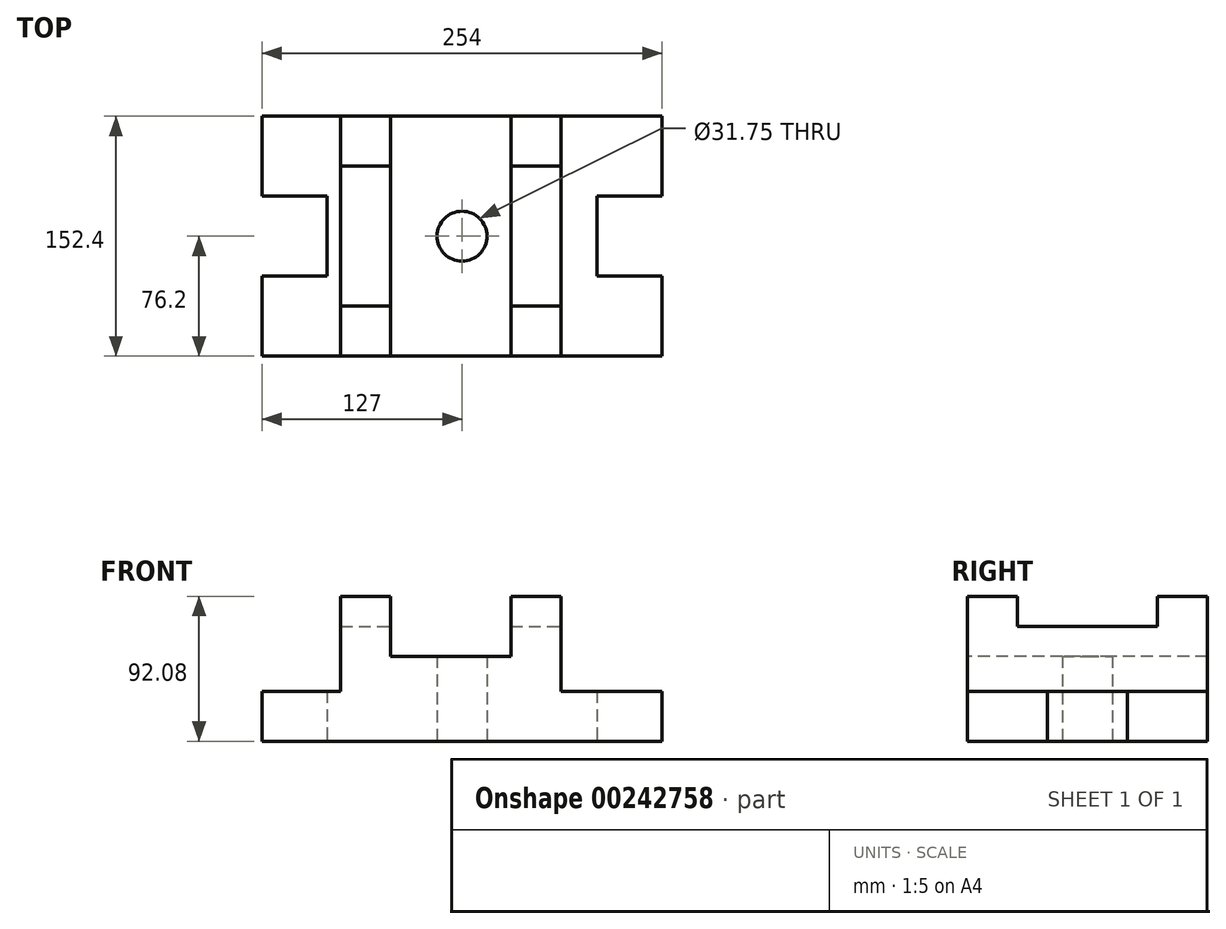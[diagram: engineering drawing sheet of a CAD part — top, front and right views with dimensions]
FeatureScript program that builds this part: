
annotation { "Feature Type Name" : "Feature", "Feature Type Description" : "" }
export const myFeature = defineFeature(function(context is Context, id is Id, definition is map)
    precondition{}
    {
        {
            var Q0;
            Q0=qCreatedBy(makeId("Top.planeOp"),FACE);
            var sketch = newSketch(context, id + "F0", { "sketchPlane" : qUnion([Q0])});
            skLineSegment(sketch, "E0.bottom", {"start": v(127, -76.2) * mm, "end": v(-127, -76.2) * mm});
            skLineSegment(sketch, "E0.top", {"start": v(127, 76.2) * mm, "end": v(-127, 76.2) * mm});
            skLineSegment(sketch, "E0.left", {"start": v(127, -76.2) * mm, "end": v(127, -25.4) * mm});
            skLineSegment(sketch, "E0.right", {"start": v(-127, -76.2) * mm, "end": v(-127, -25.4) * mm});
            skPoint(sketch, "E0.middle", {"position": v(0, 0) * mm});
            skLineSegment(sketch, "E1.bottom", {"start": v(-127, -25.4) * mm, "end": v(-85.72, -25.4) * mm});
            skLineSegment(sketch, "E1.top", {"start": v(-127, 25.4) * mm, "end": v(-85.72, 25.4) * mm});
            skLineSegment(sketch, "E1.right", {"start": v(-85.72, -25.4) * mm, "end": v(-85.72, 25.4) * mm});
            skPoint(sketch, "E1.middle", {"position": v(-106.36, 0) * mm});
            skLineSegment(sketch, "E2.bottom", {"start": v(127, -25.4) * mm, "end": v(85.72, -25.4) * mm});
            skLineSegment(sketch, "E2.top", {"start": v(127, 25.4) * mm, "end": v(85.72, 25.4) * mm});
            skLineSegment(sketch, "E2.right", {"start": v(85.72, -25.4) * mm, "end": v(85.72, 25.4) * mm});
            skPoint(sketch, "E2.middle", {"position": v(106.36, 0) * mm});
            skLineSegment(sketch, "E3.trimOffspring", {"start": v(-127, 25.4) * mm, "end": v(-127, 76.2) * mm});
            skLineSegment(sketch, "E4.trimOffspring", {"start": v(127, 25.4) * mm, "end": v(127, 76.2) * mm});
            skCircle(sketch, "E5", {"center": v(0, 0) * mm, "radius": 15.88 * mm});
            skLineSegment(sketch, "E6", {"start": v(0, 81.37) * mm, "end": v(0, 15.88) * mm, "construction": true});
            skPoint(sketch, "E6.endSnap0", {"position": v(0, -76.2) * mm});
            skLineSegment(sketch, "E7", {"start": v(-183.77, 0) * mm, "end": v(-15.88, 0) * mm, "construction": true});
            skLineSegment(sketch, "E8.trimOffspring", {"start": v(15.88, 0) * mm, "end": v(190.43, 0) * mm, "construction": true});
            skLineSegment(sketch, "E9.trimOffspring", {"start": v(0, 0) * mm, "end": v(0, -121.78) * mm, "construction": true});
            skSolve(sketch);
        }
        {
            var Q0;
            Q0=qCreatedBy(makeId("Front.planeOp"),FACE);
            var sketch = newSketch(context, id + "F1", { "sketchPlane" : qUnion([Q0])});
            skLineSegment(sketch, "E10.top", {"start": v(-77, 92.08) * mm, "end": v(-45.24, 92.08) * mm});
            skLineSegment(sketch, "E10.left", {"start": v(-77, 31.75) * mm, "end": v(-77, 92.08) * mm});
            skLineSegment(sketch, "E11.top", {"start": v(-45.24, 53.98) * mm, "end": v(0, 53.98) * mm});
            skLineSegment(sketch, "E11.left", {"start": v(-45.24, 92.08) * mm, "end": v(-45.24, 53.98) * mm});
            skPoint(sketch, "E12", {"position": v(-45.24, 92.08) * mm});
            skLineSegment(sketch, "E13.MirrorCS", {"start": v(30.96, 92.08) * mm, "end": v(30.96, 53.98) * mm});
            skLineSegment(sketch, "E14.MirrorCS", {"start": v(30.96, 53.98) * mm, "end": v(0, 53.98) * mm});
            skLineSegment(sketch, "E15.MirrorCS", {"start": v(62.7, 31.75) * mm, "end": v(62.7, 92.08) * mm});
            skLineSegment(sketch, "E16.MirrorCS", {"start": v(62.7, 92.08) * mm, "end": v(30.96, 92.08) * mm});
            skPoint(sketch, "E17.MirrorP", {"position": v(30.96, 92.08) * mm});
            skLineSegment(sketch, "E18", {"start": v(-77, 31.75) * mm, "end": v(62.7, 31.75) * mm});
            skSolve(sketch);
        }
        {
            var Q0;
            Q0=makeQuery(id+"F0.imprint","IMPRINT",FACE,{"disambiguationData":[TD([[makeQuery(id+"F0.imprint","IMPRINT",EDGE,{"derivedFrom":sQuery(id+"F0.wireOp",EDGE,"E0.bottom")}),-1.0]])]});
            extrude(context, id + "F2", {"entities" : qUnion([Q0]), "depth" : 31.75 * mm});
        }
        {
            var Q0;
            Q0 = qSketchRegion(id + "F1", true);
            extrude(context, id + "F3", {"entities" : qUnion([Q0]), "operationType" : NewBodyOperationType.ADD, "endBound" : BoundingType.SYMMETRIC, "oppositeDirection" : true, "depth" : 152.4 * mm});
        }
        {
            var Q0;
            Q0=makeQuery(id+"F3.opExtrude","SWEPT_FACE",FACE,{"disambiguationData":[OSD([sQuery(id+"F1.wireOp",EDGE,"E10.top")])]});
            var sketch = newSketch(context, id + "F4", { "sketchPlane" : qUnion([Q0])});
            skLineSegment(sketch, "E19.bottom", {"start": v(-77, 76.2) * mm, "end": v(-45.24, 76.2) * mm});
            skLineSegment(sketch, "E19.top", {"start": v(-77, 44.45) * mm, "end": v(-45.24, 44.45) * mm});
            skLineSegment(sketch, "E19.left", {"start": v(-77, 76.2) * mm, "end": v(-77, 44.45) * mm});
            skLineSegment(sketch, "E19.right", {"start": v(-45.24, 76.2) * mm, "end": v(-45.24, 44.45) * mm});
            skLineSegment(sketch, "E20.bottom", {"start": v(-77, -44.45) * mm, "end": v(-45.24, -44.45) * mm});
            skLineSegment(sketch, "E20.top", {"start": v(-77, -76.2) * mm, "end": v(-45.24, -76.2) * mm});
            skLineSegment(sketch, "E20.left", {"start": v(-77, -44.45) * mm, "end": v(-77, -76.2) * mm});
            skLineSegment(sketch, "E20.right", {"start": v(-45.24, -44.45) * mm, "end": v(-45.24, -76.2) * mm});
            skLineSegment(sketch, "E21.bottom", {"start": v(30.96, 76.2) * mm, "end": v(62.7, 76.2) * mm});
            skLineSegment(sketch, "E21.top", {"start": v(30.96, 44.45) * mm, "end": v(62.7, 44.45) * mm});
            skLineSegment(sketch, "E21.left", {"start": v(30.96, 76.2) * mm, "end": v(30.96, 44.45) * mm});
            skLineSegment(sketch, "E21.right", {"start": v(62.7, 76.2) * mm, "end": v(62.7, 44.45) * mm});
            skLineSegment(sketch, "E22.bottom", {"start": v(30.96, -76.2) * mm, "end": v(62.7, -76.2) * mm});
            skLineSegment(sketch, "E22.top", {"start": v(30.96, -44.45) * mm, "end": v(62.7, -44.45) * mm});
            skLineSegment(sketch, "E22.left", {"start": v(30.96, -76.2) * mm, "end": v(30.96, -44.45) * mm});
            skLineSegment(sketch, "E22.right", {"start": v(62.7, -76.2) * mm, "end": v(62.7, -44.45) * mm});
            skLineSegment(sketch, "E23.left", {"start": v(30.96, 44.45) * mm, "end": v(30.96, -44.45) * mm});
            skLineSegment(sketch, "E23.right", {"start": v(62.7, 44.45) * mm, "end": v(62.7, -44.45) * mm});
            skSolve(sketch);
        }
        {
            var Q0;
            {var subQ0=sQuery(id+"F4.wireOp",EDGE,"E19.top");Q0=makeQuery(id+"F4.imprint","IMPRINT",FACE,{"disambiguationData":[TD([[makeQuery(id+"F4.imprint","IMPRINT",EDGE,{"derivedFrom":subQ0}),-1.0]])]});}
            var Q1;
            Q1=makeQuery(id+"F4.imprint","IMPRINT",FACE,{"disambiguationData":[TD([[makeQuery(id+"F4.imprint","IMPRINT",EDGE,{"derivedFrom":sQuery(id+"F4.wireOp",EDGE,"E21.top")}),-1.0]])]});
            extrude(context, id + "F5", {"entities" : qUnion([Q0, Q1]), "operationType" : NewBodyOperationType.REMOVE, "oppositeDirection" : true, "depth" : 19.05 * mm});
        }
        {
            var Q0;
            Q0=makeQuery(id+"F0.imprint","IMPRINT",FACE,{"disambiguationData":[TD([[makeQuery(id+"F0.imprint","IMPRINT",EDGE,{"derivedFrom":sQuery(id+"F0.wireOp",EDGE,"E5")}),1.0]])]});
            extrude(context, id + "F6", {"entities" : qUnion([Q0]), "operationType" : NewBodyOperationType.REMOVE, "depth" : 214.38 * mm});
        }
    });
